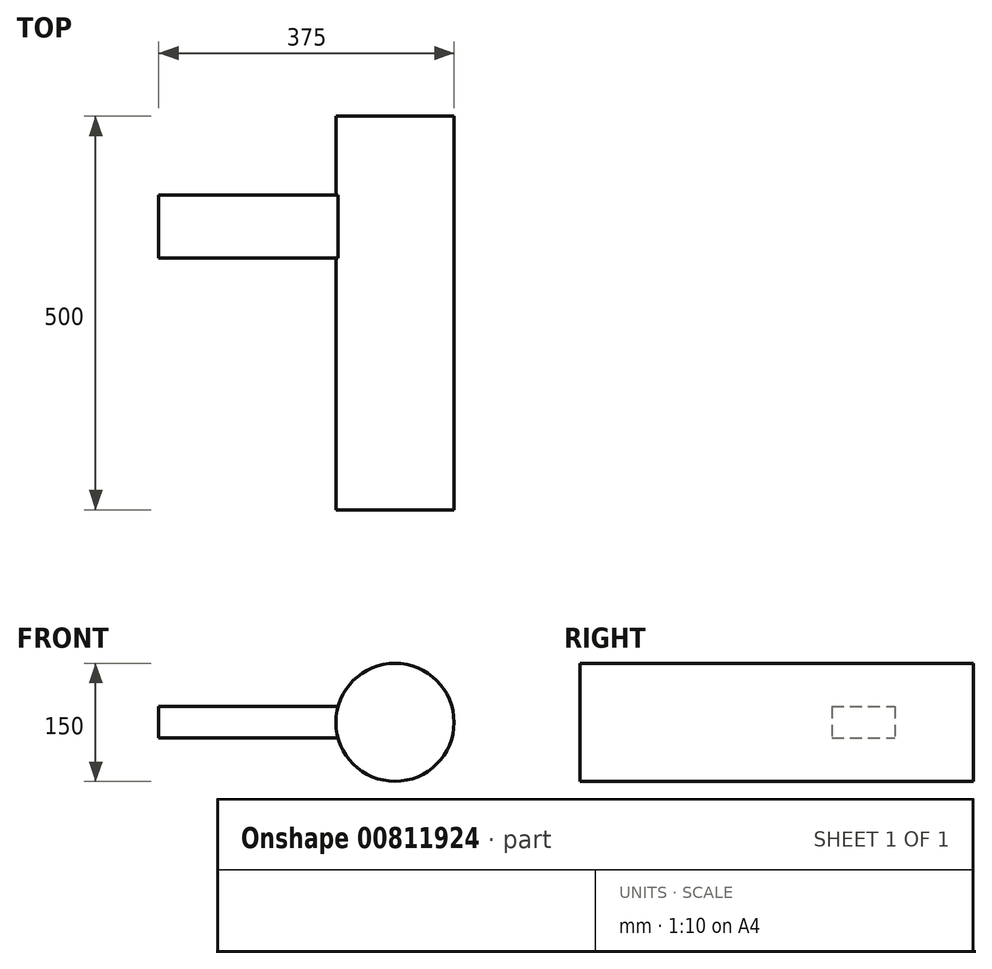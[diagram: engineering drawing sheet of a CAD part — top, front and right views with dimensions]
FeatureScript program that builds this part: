
annotation { "Feature Type Name" : "Feature", "Feature Type Description" : "" }
export const myFeature = defineFeature(function(context is Context, id is Id, definition is map)
    precondition{}
    {
        {
            var Q0;
            Q0=qCreatedBy(makeId("Front.planeOp"),FACE);
            var sketch = newSketch(context, id + "F0", { "sketchPlane" : qUnion([Q0])});
            skCircle(sketch, "E0", {"center": v(0, 0) * mm, "radius": 75 * mm});
            skSolve(sketch);
        }
        {
            var Q0;
            Q0 = qSketchRegion(id + "F0", true);
            extrude(context, id + "F1", {"entities" : qUnion([Q0]), "depth" : 500 * mm, "offsetDistance" : 25 * mm});
        }
        {
            var Q0;
            Q0=qCreatedBy(makeId("Right.planeOp"),FACE);
            var sketch = newSketch(context, id + "F2", { "sketchPlane" : qUnion([Q0])});
            skLineSegment(sketch, "E1.bottom", {"start": v(-100, 20) * mm, "end": v(-180, 20) * mm});
            skLineSegment(sketch, "E1.top", {"start": v(-100, -20) * mm, "end": v(-180, -20) * mm});
            skLineSegment(sketch, "E1.left", {"start": v(-100, 20) * mm, "end": v(-100, -20) * mm});
            skLineSegment(sketch, "E1.right", {"start": v(-180, 20) * mm, "end": v(-180, -20) * mm});
            skLineSegment(sketch, "E2", {"start": v(0, 0) * mm, "end": v(-100, 0) * mm});
            skPoint(sketch, "E2.endSnap0", {"position": v(-100, 0) * mm});
            skSolve(sketch);
        }
        {
            var Q0;
            Q0 = qSketchRegion(id + "F2", true);
            extrude(context, id + "F3", {"entities" : qUnion([Q0]), "operationType" : NewBodyOperationType.ADD, "oppositeDirection" : true, "depth" : 300 * mm, "offsetDistance" : 25 * mm});
        }
    });
